# Revit family: HL_RU_Floor drain_HL70R-A-171212
name_source: partatom
category: Instalační zařizovací předměty
units: mm (PartAtom-declared; Revit-internal decimal feet)

## family parameters
Bod výpočtu místnosti = Ano
Kóta kulaté spojky = Použít průměr
Nadpis OmniClass = Deck Waste Water Drains
Ořezat dutým tvarem při načtení = Ne
Sdílené = Ano
Typ dílu = Normální
Vždy vertikální = Ano
Založené na pracovní rovině = Ne
Číslo OmniClass = 23.70.50.21.24.14

## types (1)
- HL_Трап для внутренних помещений_HL70R
    EAN = 9003076011971
    Indexovaná poznámka = HL70R
    Komentáře k typům = Трап для внутренних помещений DN75/110 горизонтальный с предохранительным затвором обратного потока воды и тремя входными отверстиями DN40/50,с круглой насадкой d 131мм/d 112мм
    Model = HL70R
    Popis = Трап для внутренних помещений
    Přípoj CW = Ne
    Přípoj HW = Ne
    Přípoj odpadních dílů = Ano
    Přípoj ventilace = Ne
    URL = http://www.hutterer-lechner.com
    Výchozí výška = 0 mm  [stored 0 ft]
    Výrobce = HL Hutterer & Lechner GmbH
    ВЕС = 1,147 kg
    ВЫСОТА МОНТАЖА = 198 mm
    МАКСИМАЛЬНАЯ НАГРУЗКА КЛАССА = K3 - 300 kg
    МАТЕРИАЛ = PE
    НАСАДКА = 20-75mm / d 133mm / PP-V2A
    ПРИЁМНОЕ ОТВЕРСТИЕ = 3 x DN40/50
    ПРОИЗВОДИТЕЛЬНОСТЬ = 1,12 l/s
    РАЗМЕР = DN75/110
    РЕШЁТКА = d 112mm / V2A

note: [stored X ft] marks values corroborated as IEEE doubles in the binary element streams (Revit-internal decimal feet)

## geometry (parser evidence)
native form markers: Sweep x33
no freeform markers — native parametric forms only
